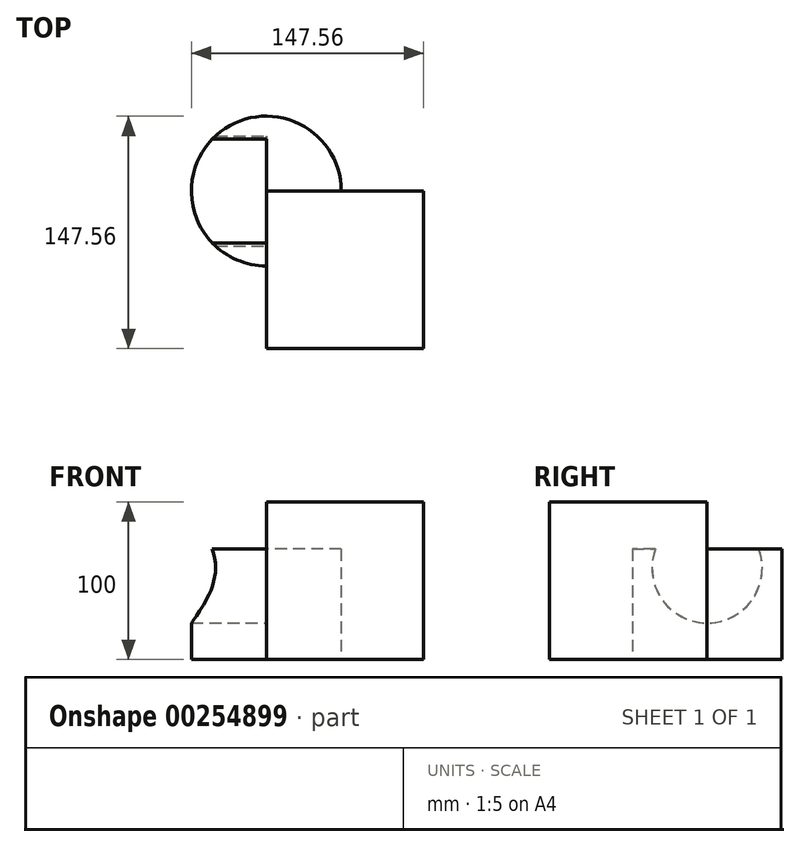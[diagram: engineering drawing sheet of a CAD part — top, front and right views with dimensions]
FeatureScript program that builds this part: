
annotation { "Feature Type Name" : "Feature", "Feature Type Description" : "" }
export const myFeature = defineFeature(function(context is Context, id is Id, definition is map)
    precondition{}
    {
        {
            var Q0;
            Q0=qCreatedBy(makeId("Front.planeOp"),FACE);
            var sketch = newSketch(context, id + "F0", { "sketchPlane" : qUnion([Q0])});
            skLineSegment(sketch, "E0.bottom", {"start": v(0, 0) * mm, "end": v(100, 0) * mm});
            skLineSegment(sketch, "E0.top", {"start": v(0, 100) * mm, "end": v(100, 100) * mm});
            skLineSegment(sketch, "E0.left", {"start": v(0, 0) * mm, "end": v(0, 100) * mm});
            skLineSegment(sketch, "E0.right", {"start": v(100, 0) * mm, "end": v(100, 100) * mm});
            skSolve(sketch);
        }
        {
            var Q0;
            Q0 = qSketchRegion(id + "F0", true);
            extrude(context, id + "F1", {"entities" : qUnion([Q0]), "depth" : 100 * mm});
        }
        {
            var Q0;
            Q0=qCreatedBy(makeId("Top.planeOp"),FACE);
            var sketch = newSketch(context, id + "F2", { "sketchPlane" : qUnion([Q0])});
            skCircle(sketch, "E1", {"center": v(0, 0) * mm, "radius": 47.4 * mm});
            skSolve(sketch);
        }
        {
            var Q0;
            Q0 = qSketchRegion(id + "F2", true);
            extrude(context, id + "F3", {"entities" : qUnion([Q0]), "operationType" : NewBodyOperationType.ADD, "depth" : 70 * mm});
        }
        {
            var Q0;
            Q0=qCreatedBy(makeId("Top.planeOp"),FACE);
            var sketch = newSketch(context, id + "F4", { "sketchPlane" : qUnion([Q0])});
            skCircle(sketch, "E2", {"center": v(0, 0) * mm, "radius": 47.56 * mm});
            skSolve(sketch);
        }
        {
            var Q0;
            Q0 = qSketchRegion(id + "F4", true);
            extrude(context, id + "F5", {"entities" : qUnion([Q0]), "operationType" : NewBodyOperationType.ADD, "depth" : 70 * mm});
        }
        {
            var Q0;
            Q0=qCreatedBy(makeId("Right.planeOp"),FACE);
            var sketch = newSketch(context, id + "F6", { "sketchPlane" : qUnion([Q0])});
            skCircle(sketch, "E3", {"center": v(0, 58.09) * mm, "radius": 35 * mm});
            skSolve(sketch);
        }
        {
            var Q0;
            Q0 = qSketchRegion(id + "F6", true);
            extrude(context, id + "F7", {"entities" : qUnion([Q0]), "operationType" : NewBodyOperationType.REMOVE, "endBound" : BoundingType.THROUGH_ALL, "oppositeDirection" : true, "depth" : 25.4 * mm});
        }
    });
